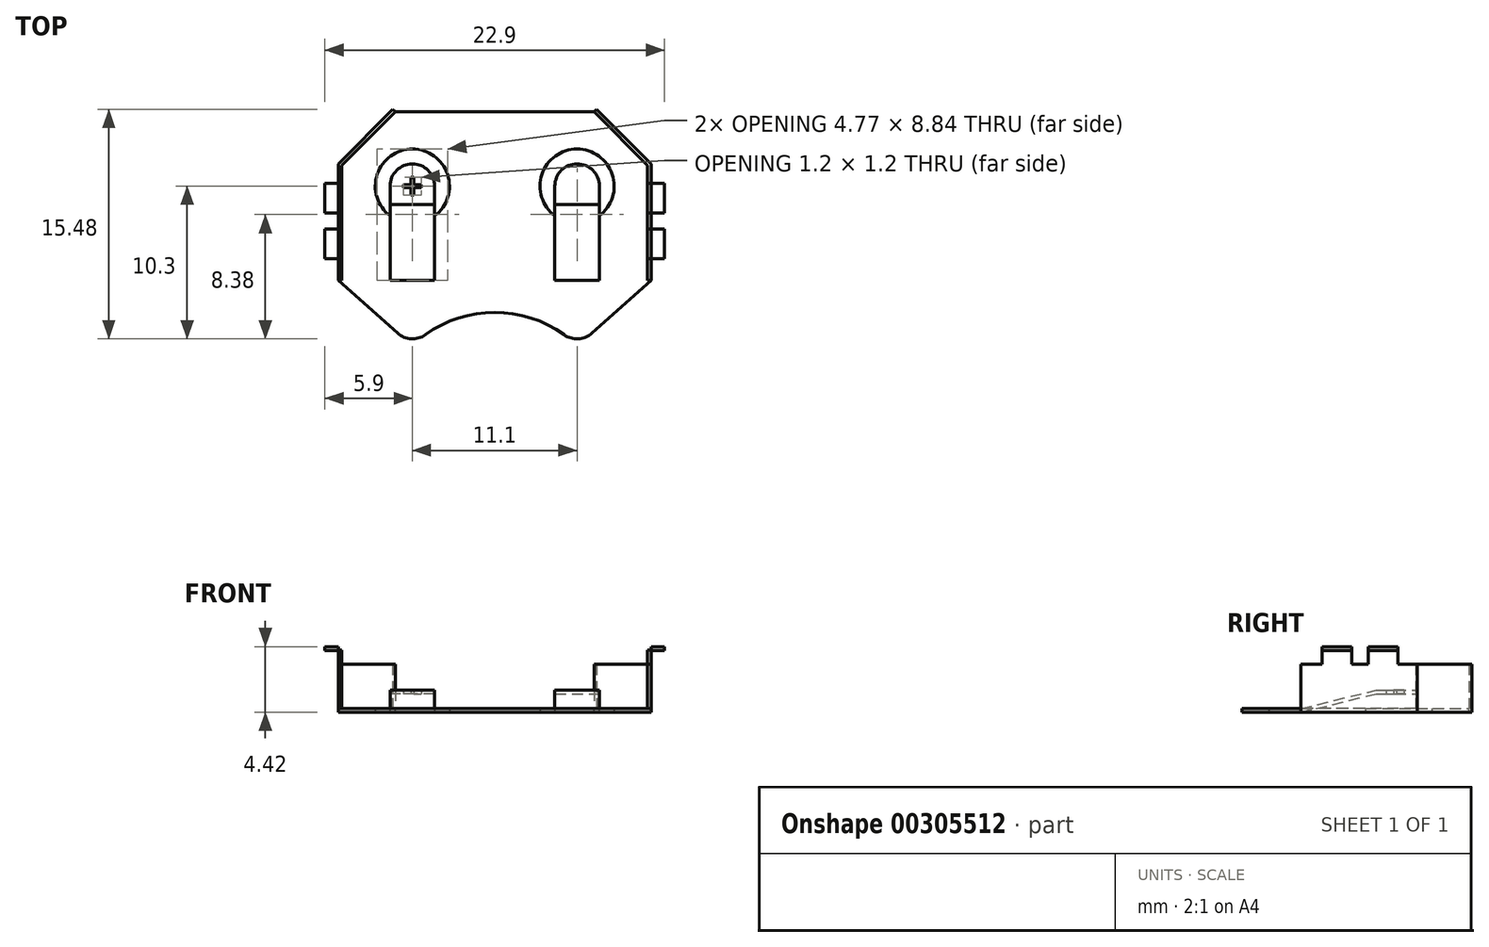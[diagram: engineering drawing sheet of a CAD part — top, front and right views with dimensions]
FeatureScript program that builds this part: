
annotation { "Feature Type Name" : "Feature", "Feature Type Description" : "" }
export const myFeature = defineFeature(function(context is Context, id is Id, definition is map)
    precondition{}
    {
        {
            var Q0;
            Q0=qCreatedBy(makeId("Top.planeOp"),FACE);
            var sketch = newSketch(context, id + "F0", { "sketchPlane" : qUnion([Q0])});
            skLineSegment(sketch, "E0.bottom", {"start": v(0, 8.01) * mm, "end": v(-7.05, 8.01) * mm});
            skLineSegment(sketch, "E0.left", {"start": v(0, 8.01) * mm, "end": v(0, -5.5) * mm});
            skLineSegment(sketch, "E0.right", {"start": v(-10.55, 4.51) * mm, "end": v(-10.55, -3.33) * mm});
            skLineSegment(sketch, "E1", {"start": v(-10.55, 4.51) * mm, "end": v(-7.05, 8.01) * mm});
            skArc(sketch, "E2", {"start": v(-4.05, 1.01) * mm, "mid": v(-5.55, 5.51) * mm, "end": v(-7.05, 1.01) * mm});
            skArc(sketch, "E3", {"start": v(-6.55, -6.9) * mm, "mid": v(-5.63, -7.29) * mm, "end": v(-4.67, -7) * mm});
            skArc(sketch, "E4", {"start": v(0, -5.5) * mm, "mid": v(-2.46, -5.89) * mm, "end": v(-4.67, -7) * mm});
            skLineSegment(sketch, "E5", {"start": v(0, -5.5) * mm, "end": v(1, -5.5) * mm, "construction": true});
            skPoint(sketch, "E6.orphan", {"position": v(-5, -7.26) * mm});
            skLineSegment(sketch, "E7", {"start": v(-6.55, -6.9) * mm, "end": v(-10.55, -3.33) * mm});
            skLineSegment(sketch, "E8.top", {"start": v(-7.05, -3.33) * mm, "end": v(-4.05, -3.33) * mm});
            skLineSegment(sketch, "E8.left", {"start": v(-7.05, 1.01) * mm, "end": v(-7.05, -3.33) * mm});
            skLineSegment(sketch, "E8.right", {"start": v(-4.05, 1.01) * mm, "end": v(-4.05, -3.33) * mm});
            skArc(sketch, "E9", {"start": v(-4.05, 3.01) * mm, "mid": v(-5.55, 4.51) * mm, "end": v(-7.05, 3.01) * mm, "construction": true});
            skLineSegment(sketch, "E10", {"start": v(-7.05, 1.01) * mm, "end": v(-7.05, 3.01) * mm, "construction": true});
            skLineSegment(sketch, "E11", {"start": v(-4.05, 1.01) * mm, "end": v(-4.05, 3.01) * mm, "construction": true});
            skSolve(sketch);
        }
        {
            var Q0;
            Q0 = qSketchRegion(id + "F0", true);
            extrude(context, id + "F1", {"entities" : qUnion([Q0]), "depth" : .25 * mm});
        }
        {
            var Q0;
            Q0=makeQuery(id+"F1.opExtrude","CAP_FACE",FACE,{"disambiguationData":[OSD([sQuery(id+"F0.wireOp",EDGE,"E0.bottom"),sQuery(id+"F0.wireOp",EDGE,"E0.left"),sQuery(id+"F0.wireOp",EDGE,"E0.right"),sQuery(id+"F0.wireOp",EDGE,"E1"),sQuery(id+"F0.wireOp",EDGE,"E2"),sQuery(id+"F0.wireOp",EDGE,"E3"),sQuery(id+"F0.wireOp",EDGE,"E4"),sQuery(id+"F0.wireOp",EDGE,"E7"),sQuery(id+"F0.wireOp",EDGE,"E8.top"),sQuery(id+"F0.wireOp",EDGE,"E8.left"),sQuery(id+"F0.wireOp",EDGE,"E8.right")])],"isStart":false});
            var sketch = newSketch(context, id + "F2", { "sketchPlane" : qUnion([Q0])});
            skLineSegment(sketch, "E12.0", {"start": v(-10.55, 4.51) * mm, "end": v(-10.55, -3.33) * mm});
            skLineSegment(sketch, "E12.1", {"start": v(-10.55, 4.51) * mm, "end": v(-7.05, 8.01) * mm});
            skLineSegment(sketch, "E13.0", {"start": v(-10.3, 4.4) * mm, "end": v(-10.3, -3.33) * mm});
            skLineSegment(sketch, "E13.1", {"start": v(-10.3, 4.4) * mm, "end": v(-6.7, 8.01) * mm});
            skLineSegment(sketch, "E14", {"start": v(-10.55, -3.33) * mm, "end": v(-10.3, -3.33) * mm});
            skLineSegment(sketch, "E15", {"start": v(-6.7, 8.01) * mm, "end": v(-6.87, 8.19) * mm});
            skLineSegment(sketch, "E16", {"start": v(-7.05, 8.01) * mm, "end": v(-6.87, 8.19) * mm});
            skSolve(sketch);
        }
        {
            var Q0;
            Q0=makeQuery(id+"F2.imprint","IMPRINT",FACE,{"disambiguationData":[TD([[makeQuery(id+"F2.imprint","IMPRINT",EDGE,{"derivedFrom":sQuery(id+"F2.wireOp",EDGE,"E13.0")}),1.0]])]});
            var sketch = newSketch(context, id + "F3", { "sketchPlane" : qUnion([Q0])});
            skLineSegment(sketch, "E17.0", {"start": v(-10.55, 4.51) * mm, "end": v(-10.55, -3.33) * mm, "construction": true});
            skLineSegment(sketch, "E18.bottom", {"start": v(-10.55, 3.21) * mm, "end": v(-10.3, 3.21) * mm});
            skLineSegment(sketch, "E18.top", {"start": v(-10.55, 1.21) * mm, "end": v(-10.3, 1.21) * mm});
            skLineSegment(sketch, "E18.left", {"start": v(-10.55, 3.21) * mm, "end": v(-10.55, 1.21) * mm});
            skLineSegment(sketch, "E18.right", {"start": v(-10.3, 3.21) * mm, "end": v(-10.3, 1.21) * mm});
            skLineSegment(sketch, "E19.bottom", {"start": v(-10.55, 0.11) * mm, "end": v(-10.3, 0.11) * mm});
            skLineSegment(sketch, "E19.top", {"start": v(-10.55, -1.89) * mm, "end": v(-10.3, -1.89) * mm});
            skLineSegment(sketch, "E19.left", {"start": v(-10.55, 0.11) * mm, "end": v(-10.55, -1.89) * mm});
            skLineSegment(sketch, "E19.right", {"start": v(-10.3, 0.11) * mm, "end": v(-10.3, -1.89) * mm});
            skSolve(sketch);
        }
        {
            var Q0;
            Q0 = qSketchRegion(id + "F3", true);
            extrude(context, id + "F4", {"entities" : qUnion([Q0]), "operationType" : NewBodyOperationType.ADD, "depth" : (4.2 - .25) * mm});
        }
        {
            var Q0;
            Q0=makeQuery(id+"F4.boolean.opBoolean","MERGE",FACE,{"derivedFrom":[makeQuery(id+"F1.opExtrude","SWEPT_FACE",FACE,{"disambiguationData":[OSD([sQuery(id+"F0.wireOp",EDGE,"E0.right")])]}),makeQuery(id+"F4.opExtrude","SWEPT_FACE",FACE,{"disambiguationData":[OSD([sQuery(id+"F3.wireOp",EDGE,"E18.left")])]}),makeQuery(id+"F4.opExtrude","SWEPT_FACE",FACE,{"disambiguationData":[OSD([sQuery(id+"F3.wireOp",EDGE,"E19.left")])]})]});
            var sketch = newSketch(context, id + "F5", { "sketchPlane" : qUnion([Q0])});
            skLineSegment(sketch, "E20.0", {"start": v(-3.21, 4.42) * mm, "end": v(-1.21, 4.42) * mm});
            skLineSegment(sketch, "E20.1", {"start": v(-0.11, 4.42) * mm, "end": v(1.89, 4.42) * mm});
            skLineSegment(sketch, "E21.0", {"start": v(-3.21, 4.17) * mm, "end": v(-1.21, 4.17) * mm});
            skLineSegment(sketch, "E22", {"start": v(-1.21, 4.17) * mm, "end": v(-1.21, 4.42) * mm});
            skLineSegment(sketch, "E23", {"start": v(-3.21, 4.17) * mm, "end": v(-3.21, 4.42) * mm});
            skLineSegment(sketch, "E24.0", {"start": v(-0.11, 4.17) * mm, "end": v(1.89, 4.17) * mm});
            skLineSegment(sketch, "E25", {"start": v(-0.11, 4.17) * mm, "end": v(-0.11, 4.42) * mm});
            skLineSegment(sketch, "E26", {"start": v(1.89, 4.17) * mm, "end": v(1.89, 4.42) * mm});
            skSolve(sketch);
        }
        {
            var Q0;
            Q0 = qSketchRegion(id + "F5", true);
            extrude(context, id + "F6", {"entities" : qUnion([Q0]), "operationType" : NewBodyOperationType.ADD, "depth" : .9 * mm});
        }
        {
            var Q0;
            Q0 = qSketchRegion(id + "F2", true);
            extrude(context, id + "F7", {"entities" : qUnion([Q0]), "operationType" : NewBodyOperationType.ADD, "depth" : 3 * mm});
        }
        {
            var Q0;
            Q0=makeQuery(id+"F7.opExtrude","CAP_FACE",FACE,{"disambiguationData":[OSD([sQuery(id+"F2.wireOp",EDGE,"E12.0"),sQuery(id+"F2.wireOp",EDGE,"E12.1"),sQuery(id+"F2.wireOp",EDGE,"E13.0"),sQuery(id+"F2.wireOp",EDGE,"E13.1"),sQuery(id+"F2.wireOp",EDGE,"E14"),sQuery(id+"F2.wireOp",EDGE,"E15"),sQuery(id+"F2.wireOp",EDGE,"E16")])],"isStart":true});
            var Q1;
            Q1=makeQuery(id+"F1.opExtrude","CAP_FACE",FACE,{"disambiguationData":[OSD([sQuery(id+"F0.wireOp",EDGE,"E0.bottom"),sQuery(id+"F0.wireOp",EDGE,"E0.left"),sQuery(id+"F0.wireOp",EDGE,"E0.right"),sQuery(id+"F0.wireOp",EDGE,"E1"),sQuery(id+"F0.wireOp",EDGE,"E2"),sQuery(id+"F0.wireOp",EDGE,"E3"),sQuery(id+"F0.wireOp",EDGE,"E4"),sQuery(id+"F0.wireOp",EDGE,"E7"),sQuery(id+"F0.wireOp",EDGE,"E8.top"),sQuery(id+"F0.wireOp",EDGE,"E8.left"),sQuery(id+"F0.wireOp",EDGE,"E8.right")])],"isStart":true});
            extrude(context, id + "F8", {"entities" : qUnion([Q0]), "operationType" : NewBodyOperationType.ADD, "endBound" : BoundingType.UP_TO_SURFACE, "endBoundEntityFace" : qUnion([Q1]), "depth" : 25 * mm});
        }
        {
            var Q0;
            Q0=makeQuery(id+"F1.opExtrude","SWEPT_FACE",FACE,{"disambiguationData":[OSD([sQuery(id+"F0.wireOp",EDGE,"E8.left")])]});
            var sketch = newSketch(context, id + "F9", { "sketchPlane" : qUnion([Q0])});
            skLineSegment(sketch, "E27.0", {"start": v(-3.33, 0.25) * mm, "end": v(-3.33, 0) * mm});
            skLineSegment(sketch, "E28", {"start": v(-3.33, 0.25) * mm, "end": v(1.76, 1.5) * mm});
            skLineSegment(sketch, "E29", {"start": v(-3.33, 0) * mm, "end": v(1.76, 1.25) * mm});
            skLineSegment(sketch, "E30", {"start": v(1.76, 1.25) * mm, "end": v(1.76, 1.5) * mm});
            skSolve(sketch);
        }
        {
            var Q0;
            Q0 = qSketchRegion(id + "F9", true);
            var Q1;
            Q1=makeQuery(id+"F1.opExtrude","SWEPT_FACE",FACE,{"disambiguationData":[OSD([sQuery(id+"F0.wireOp",EDGE,"E8.right")])]});
            extrude(context, id + "F10", {"entities" : qUnion([Q0]), "operationType" : NewBodyOperationType.ADD, "endBound" : BoundingType.UP_TO_SURFACE, "endBoundEntityFace" : qUnion([Q1]), "depth" : 25 * mm});
        }
        {
            var Q0;
            Q0=makeQuery(id+"F10.opExtrude","SWEPT_EDGE",EDGE,{"disambiguationData":[OSD([sQuery(id+"F9.wireOp",EDGE,"E29"),sQuery(id+"F9.wireOp",EDGE,"E30")])]});
            cPoint(context, id + "F11", {"entities" : qUnion([Q0]), "parameter" : 0.5});
        }
        {
            var Q0;
            Q0=makeQuery(id+"F1.opExtrude","CAP_FACE",FACE,{"disambiguationData":[OSD([sQuery(id+"F0.wireOp",EDGE,"E0.bottom"),sQuery(id+"F0.wireOp",EDGE,"E0.left"),sQuery(id+"F0.wireOp",EDGE,"E0.right"),sQuery(id+"F0.wireOp",EDGE,"E1"),sQuery(id+"F0.wireOp",EDGE,"E2"),sQuery(id+"F0.wireOp",EDGE,"E3"),sQuery(id+"F0.wireOp",EDGE,"E4"),sQuery(id+"F0.wireOp",EDGE,"E7"),sQuery(id+"F0.wireOp",EDGE,"E8.top"),sQuery(id+"F0.wireOp",EDGE,"E8.left"),sQuery(id+"F0.wireOp",EDGE,"E8.right")])],"isStart":false});
            var Q1;
            Q1 = qCreatedBy(id + "F11" ,VERTEX);
            cPlane(context, id + "F12", {"entities" : qUnion([Q0, Q1]), "cplaneType" : CPlaneType.PLANE_POINT, "offset" : 25 * mm, "width" : 150 * mm, "height" : 150 * mm});
        }
        {
            var Q0;
            Q0=qCreatedBy(id+"F12.planeOp",FACE);
            var sketch = newSketch(context, id + "F13", { "sketchPlane" : qUnion([Q0])});
            skArc(sketch, "E31.0", {"start": v(-4.05, 3.01) * mm, "mid": v(-5.55, 4.51) * mm, "end": v(-7.05, 3.01) * mm});
            skLineSegment(sketch, "E32.0", {"start": v(-4.05, 1.76) * mm, "end": v(-7.05, 1.76) * mm});
            skLineSegment(sketch, "E33", {"start": v(-7.05, 1.76) * mm, "end": v(-7.05, 3.01) * mm});
            skLineSegment(sketch, "E34", {"start": v(-4.05, 1.76) * mm, "end": v(-4.05, 3.01) * mm});
            skSolve(sketch);
        }
        {
            var Q0;
            Q0 = qSketchRegion(id + "F13", true);
            var Q1;
            Q1=makeQuery(id+"F10.opExtrude","CAP_VERTEX",VERTEX,{"disambiguationData":[OSD([sQuery(id+"F0.wireOp",EDGE,"E8.right"),sQuery(id+"F9.wireOp",EDGE,"E28"),sQuery(id+"F9.wireOp",EDGE,"E30")])],"isStart":false});
            extrude(context, id + "F14", {"entities" : qUnion([Q0]), "operationType" : NewBodyOperationType.ADD, "endBound" : BoundingType.UP_TO_VERTEX, "endBoundEntityVertex" : qUnion([Q1]), "depth" : 25 * mm});
        }
        {
            var Q0;
            Q0=makeQuery(id+"F1.opExtrude","SWEPT_BODY",BODY,{"disambiguationData":[OSD([sQuery(id+"F0.wireOp",EDGE,"E0.bottom"),sQuery(id+"F0.wireOp",EDGE,"E0.left"),sQuery(id+"F0.wireOp",EDGE,"E0.right"),sQuery(id+"F0.wireOp",EDGE,"E1"),sQuery(id+"F0.wireOp",EDGE,"E2"),sQuery(id+"F0.wireOp",EDGE,"E3"),sQuery(id+"F0.wireOp",EDGE,"E4"),sQuery(id+"F0.wireOp",EDGE,"E7"),sQuery(id+"F0.wireOp",EDGE,"E8.top"),sQuery(id+"F0.wireOp",EDGE,"E8.left"),sQuery(id+"F0.wireOp",EDGE,"E8.right")])]});
            var Q1;
            Q1=makeQuery(id+"F1.opExtrude","SWEPT_FACE",FACE,{"disambiguationData":[OSD([sQuery(id+"F0.wireOp",EDGE,"E0.left")])]});
            mirror(context, id + "F15", {"operationType" : NewBodyOperationType.ADD, "entities" : qUnion([Q0]), "mirrorPlane" : qUnion([Q1])});
        }
        {
            var Q0;
            Q0=makeQuery(id+"F14.opExtrude","CAP_FACE",FACE,{"disambiguationData":[OSD([sQuery(id+"F13.wireOp",EDGE,"E31.0"),sQuery(id+"F13.wireOp",EDGE,"E32.0"),sQuery(id+"F13.wireOp",EDGE,"E33"),sQuery(id+"F13.wireOp",EDGE,"E34")])],"isStart":true});
            var sketch = newSketch(context, id + "F16", { "sketchPlane" : qUnion([Q0])});
            skLineSegment(sketch, "E35", {"start": v(-5.55, -4.51) * mm, "end": v(-5.55, -3.01) * mm, "construction": true});
            skLineSegment(sketch, "E36", {"start": v(-5.55, -3.01) * mm, "end": v(-4.05, -3.01) * mm, "construction": true});
            skLineSegment(sketch, "E37", {"start": v(-5.55, -3.61) * mm, "end": v(-5.45, -3.61) * mm});
            skLineSegment(sketch, "E38", {"start": v(-5.45, -3.61) * mm, "end": v(-5.45, -3.11) * mm});
            skLineSegment(sketch, "E39", {"start": v(-5.45, -3.11) * mm, "end": v(-4.95, -3.11) * mm});
            skLineSegment(sketch, "E40", {"start": v(-4.95, -3.11) * mm, "end": v(-4.95, -3.01) * mm});
            skLineSegment(sketch, "E41.MirrorCS", {"start": v(-5.55, -3.61) * mm, "end": v(-5.65, -3.61) * mm});
            skLineSegment(sketch, "E42.MirrorCS", {"start": v(-5.65, -3.61) * mm, "end": v(-5.65, -3.11) * mm});
            skLineSegment(sketch, "E43.MirrorCS", {"start": v(-5.65, -3.11) * mm, "end": v(-6.15, -3.11) * mm});
            skLineSegment(sketch, "E44.MirrorCS", {"start": v(-6.15, -3.11) * mm, "end": v(-6.15, -3.01) * mm});
            skLineSegment(sketch, "E45.MirrorCS", {"start": v(-4.95, -2.91) * mm, "end": v(-4.95, -3.01) * mm});
            skLineSegment(sketch, "E46.MirrorCS", {"start": v(-5.45, -2.91) * mm, "end": v(-4.95, -2.91) * mm});
            skLineSegment(sketch, "E47.MirrorCS", {"start": v(-5.45, -2.41) * mm, "end": v(-5.45, -2.91) * mm});
            skLineSegment(sketch, "E48.MirrorCS", {"start": v(-5.55, -2.41) * mm, "end": v(-5.45, -2.41) * mm});
            skLineSegment(sketch, "E49.MirrorCS", {"start": v(-5.55, -2.41) * mm, "end": v(-5.65, -2.41) * mm});
            skLineSegment(sketch, "E50.MirrorCS", {"start": v(-5.65, -2.41) * mm, "end": v(-5.65, -2.91) * mm});
            skLineSegment(sketch, "E51.MirrorCS", {"start": v(-5.65, -2.91) * mm, "end": v(-6.15, -2.91) * mm});
            skLineSegment(sketch, "E52.MirrorCS", {"start": v(-6.15, -2.91) * mm, "end": v(-6.15, -3.01) * mm});
            skSolve(sketch);
        }
        {
            var Q0;
            Q0 = qSketchRegion(id + "F16", true);
            extrude(context, id + "F17", {"entities" : qUnion([Q0]), "operationType" : NewBodyOperationType.REMOVE, "oppositeDirection" : true, "depth" : .25 * mm});
        }
    });
